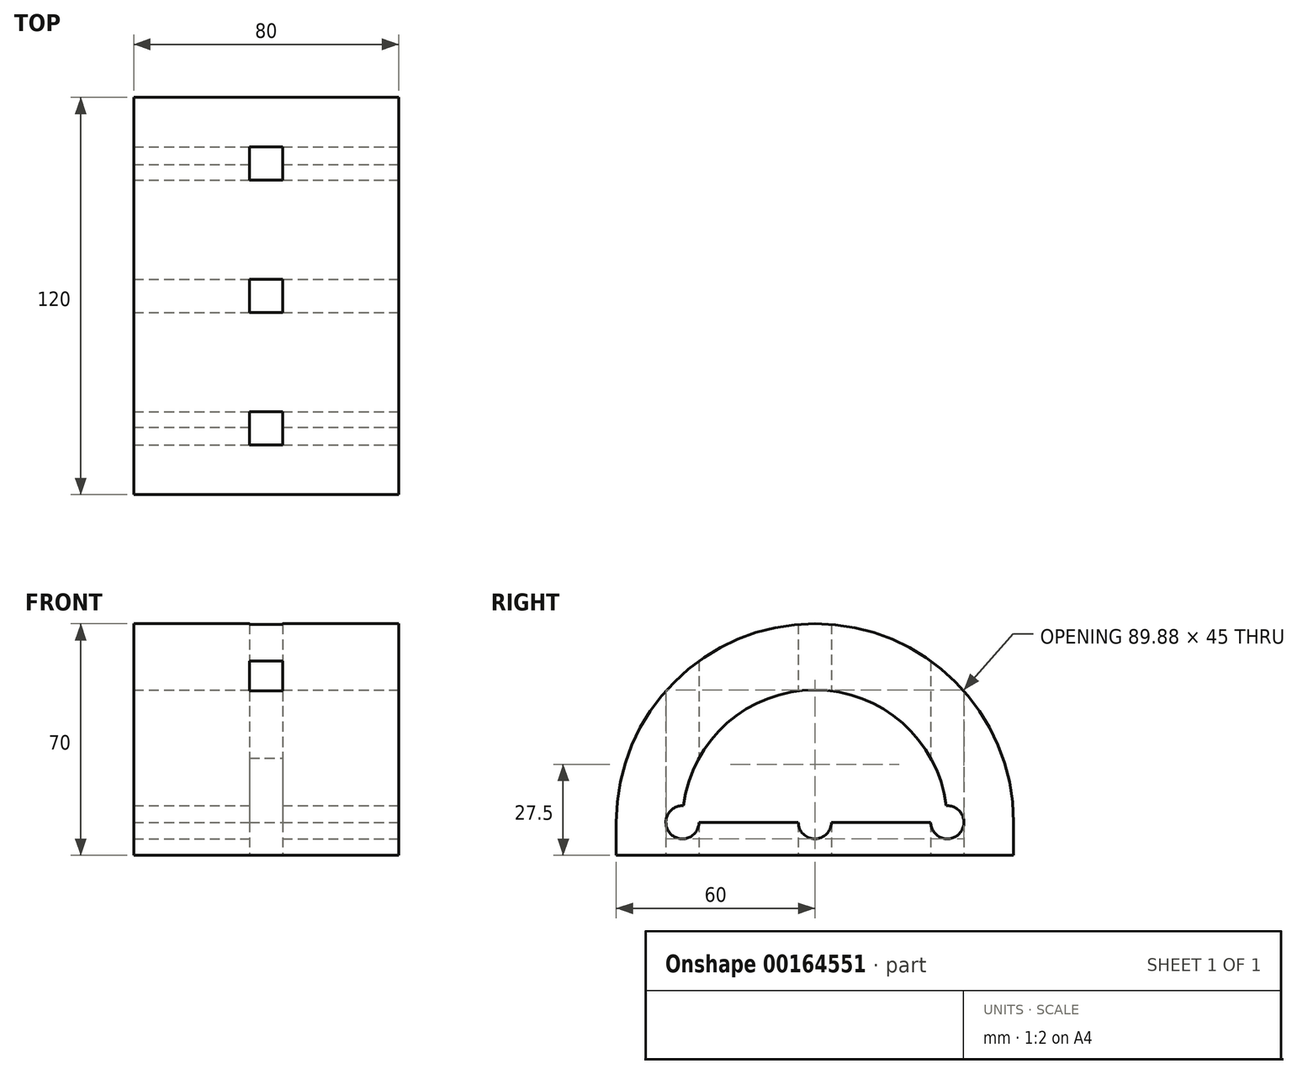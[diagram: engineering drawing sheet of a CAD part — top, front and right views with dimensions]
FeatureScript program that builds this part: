
annotation { "Feature Type Name" : "Feature", "Feature Type Description" : "" }
export const myFeature = defineFeature(function(context is Context, id is Id, definition is map)
    precondition{}
    {
        {
            var Q0;
            Q0=qCreatedBy(makeId("Right.planeOp"),FACE);
            var sketch = newSketch(context, id + "F0", { "sketchPlane" : qUnion([Q0])});
            skLineSegment(sketch, "E0.bottom", {"start": v(-60, -5) * mm, "end": v(60, -5) * mm});
            skLineSegment(sketch, "E0.top", {"start": v(-60, 5) * mm, "end": v(60, 5) * mm});
            skLineSegment(sketch, "E0.left", {"start": v(-60, -5) * mm, "end": v(-60, 5) * mm});
            skLineSegment(sketch, "E0.right", {"start": v(60, -5) * mm, "end": v(60, 5) * mm});
            skPoint(sketch, "E0.middle", {"position": v(0, 0) * mm});
            skArc(sketch, "E1", {"start": v(60, 5) * mm, "mid": v(0, 65) * mm, "end": v(-60, 5) * mm});
            skSolve(sketch);
        }
        {
            var Q0;
            Q0=qSketchRegion(id+"F0",true);
            extrude(context, id + "F1", {"entities" : qUnion([Q0]), "depth" : 80 * mm});
        }
        {
            var Q0;
            Q0=makeQuery(id+"F1.opExtrude","CAP_FACE",FACE,{"disambiguationData":[OSD([sQuery(id+"F0.wireOp",EDGE,"E0.bottom"),sQuery(id+"F0.wireOp",EDGE,"E0.left"),sQuery(id+"F0.wireOp",EDGE,"E0.right"),sQuery(id+"F0.wireOp",EDGE,"E1")])],"isStart":false});
            var sketch = newSketch(context, id + "F2", { "sketchPlane" : qUnion([Q0])});
            skCircle(sketch, "E2", {"center": v(0, 5) * mm, "radius": 5 * mm});
            skCircle(sketch, "E3", {"center": v(40, 5) * mm, "radius": 5 * mm});
            skCircle(sketch, "E4", {"center": v(-40, 5) * mm, "radius": 5 * mm});
            skArc(sketch, "E5", {"start": v(40, 5) * mm, "mid": v(0, 45) * mm, "end": v(-40, 5) * mm});
            skLineSegment(sketch, "E6", {"start": v(-40, 5) * mm, "end": v(40, 5) * mm});
            skSolve(sketch);
        }
        {
            var Q0;
            Q0=qSketchRegion(id+"F2",true);
            extrude(context, id + "F3", {"entities" : qUnion([Q0]), "operationType" : NewBodyOperationType.REMOVE, "endBound" : BoundingType.THROUGH_ALL, "oppositeDirection" : true, "depth" : 25 * mm});
        }
        {
            var Q0;
            Q0=qSketchRegion(id+"F2",true);
            extrude(context, id + "F4", {"entities" : qUnion([Q0]), "operationType" : NewBodyOperationType.REMOVE, "oppositeDirection" : true, "depth" : 25 * mm});
        }
        {
            var Q0;
            Q0=makeQuery(id+"F1.opExtrude","SWEPT_FACE",FACE,{"disambiguationData":[OSD([sQuery(id+"F0.wireOp",EDGE,"E0.bottom")])]});
            var sketch = newSketch(context, id + "F5", { "sketchPlane" : qUnion([Q0])});
            skLineSegment(sketch, "E7.bottom", {"start": v(35, 35) * mm, "end": v(45, 35) * mm});
            skLineSegment(sketch, "E7.top", {"start": v(35, 45) * mm, "end": v(45, 45) * mm});
            skLineSegment(sketch, "E7.left", {"start": v(35, 35) * mm, "end": v(35, 45) * mm});
            skLineSegment(sketch, "E7.right", {"start": v(45, 35) * mm, "end": v(45, 45) * mm});
            skPoint(sketch, "E7.middle", {"position": v(40, 40) * mm});
            skPoint(sketch, "E7.middle.positionSnap0", {"position": v(40, 60) * mm});
            skPoint(sketch, "E7.centerSnap0", {"position": v(40, 60) * mm});
            skLineSegment(sketch, "E8.bottom", {"start": v(35, -5) * mm, "end": v(45, -5) * mm});
            skLineSegment(sketch, "E8.top", {"start": v(35, 5) * mm, "end": v(45, 5) * mm});
            skLineSegment(sketch, "E8.left", {"start": v(35, -5) * mm, "end": v(35, 5) * mm});
            skLineSegment(sketch, "E8.right", {"start": v(45, -5) * mm, "end": v(45, 5) * mm});
            skPoint(sketch, "E8.middle", {"position": v(40, 0) * mm});
            skLineSegment(sketch, "E9.bottom", {"start": v(45, -35) * mm, "end": v(35, -35) * mm});
            skLineSegment(sketch, "E9.top", {"start": v(45, -45) * mm, "end": v(35, -45) * mm});
            skLineSegment(sketch, "E9.left", {"start": v(45, -35) * mm, "end": v(45, -45) * mm});
            skLineSegment(sketch, "E9.right", {"start": v(35, -35) * mm, "end": v(35, -45) * mm});
            skPoint(sketch, "E9.middle", {"position": v(40, -40) * mm});
            skSolve(sketch);
        }
        {
            var Q0;
            Q0=qSketchRegion(id+"F5",true);
            extrude(context, id + "F6", {"entities" : qUnion([Q0]), "operationType" : NewBodyOperationType.REMOVE, "endBound" : BoundingType.THROUGH_ALL, "oppositeDirection" : true, "depth" : 25 * mm});
        }
    });
